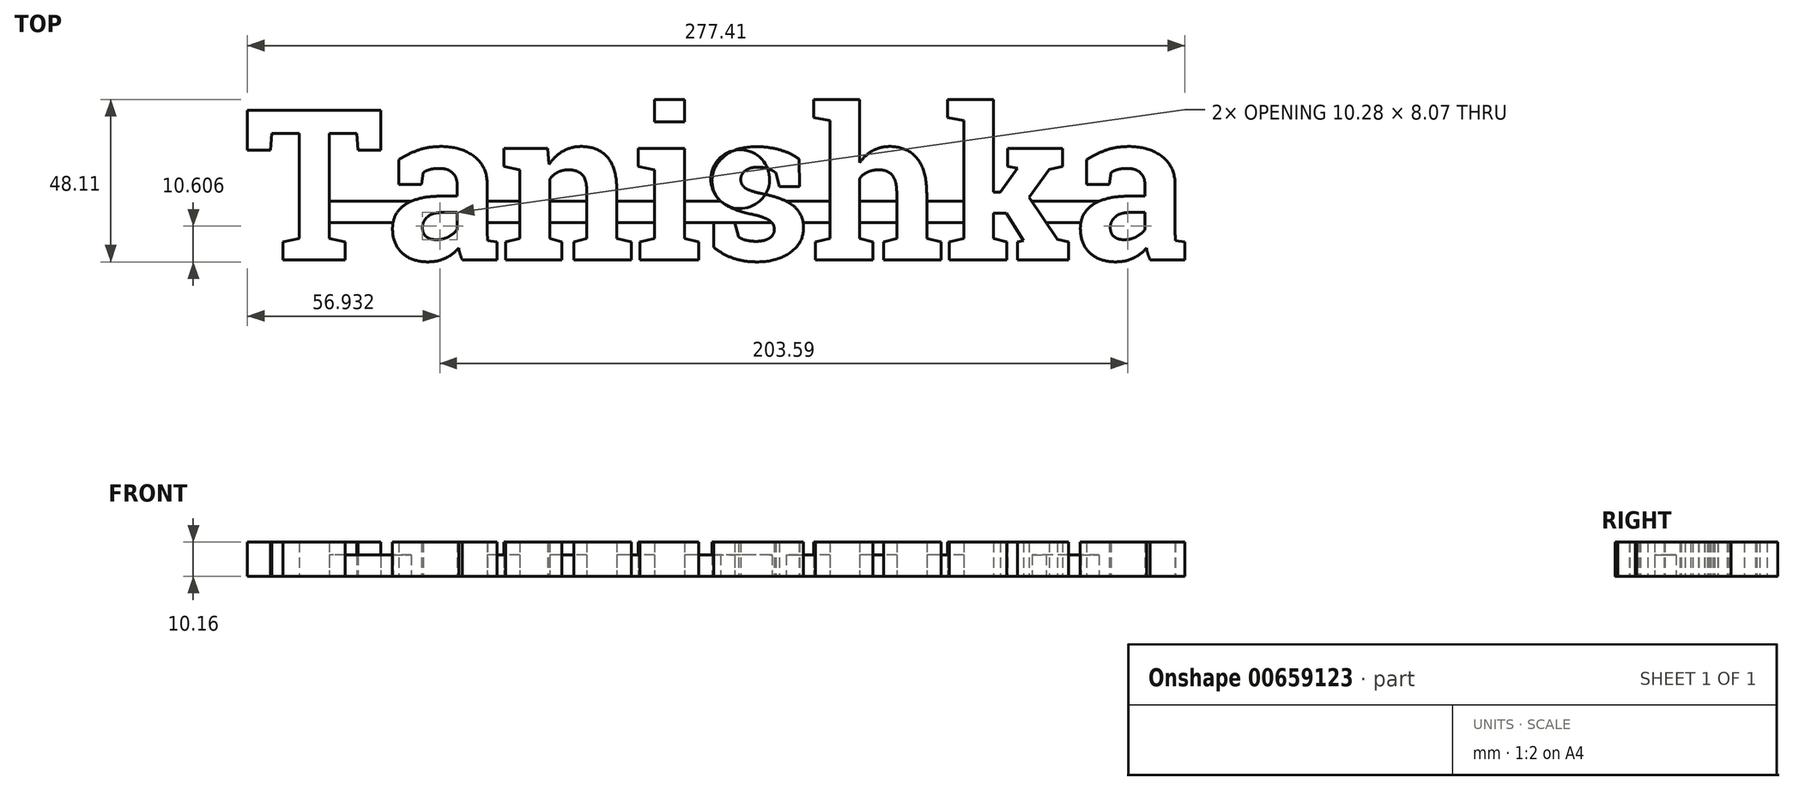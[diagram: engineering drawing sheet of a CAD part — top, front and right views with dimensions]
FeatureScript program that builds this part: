
annotation { "Feature Type Name" : "Feature", "Feature Type Description" : "" }
export const myFeature = defineFeature(function(context is Context, id is Id, definition is map)
    precondition{}
    {
        {
            var Q0;
            Q0=qCreatedBy(makeId("Top.planeOp"),FACE);
            var sketch = newSketch(context, id + "F0", { "sketchPlane" : qUnion([Q0])});
            skText(sketch, "E0", { "text": "Tanishka", "fontName": "RobotoSlab-Bold.ttf"});
            skLineSegment(sketch, "E1.bottom", {"start": v(206.32, -10.13) * mm, "end": v(-38.92, -10.13) * mm});
            skLineSegment(sketch, "E1.top", {"start": v(206.32, -3.78) * mm, "end": v(-38.92, -3.78) * mm});
            skLineSegment(sketch, "E1.left", {"start": v(206.32, -10.13) * mm, "end": v(206.32, -3.78) * mm});
            skLineSegment(sketch, "E1.right", {"start": v(-38.92, -10.13) * mm, "end": v(-38.92, -3.78) * mm});
            skPoint(sketch, "E1.middle", {"position": v(83.7, -6.96) * mm});
            skLineSegment(sketch, "E2.bottom", {"start": v(72.26, 26.44) * mm, "end": v(67.18, 26.44) * mm});
            skLineSegment(sketch, "E2.top", {"start": v(72.26, 10.06) * mm, "end": v(67.18, 10.06) * mm});
            skLineSegment(sketch, "E2.left", {"start": v(72.26, 26.44) * mm, "end": v(72.26, 10.06) * mm});
            skLineSegment(sketch, "E2.right", {"start": v(67.18, 26.44) * mm, "end": v(67.18, 10.06) * mm});
            const initialGuessF0  = {"E0": [-0.05753, -0.0211, 1, 0, 0.04487]};
            skSetInitialGuess(sketch, initialGuessF0);
            skSolve(sketch);
        }
        {
            var Q0;
            {var subQ0=sQuery(id+"F0.wireOp",EDGE,"E0.sketch_text.stroke-88");Q0=makeQuery(id+"F0.imprint","IMPRINT",FACE,{"disambiguationData":[TD([[makeQuery(id+"F0.imprint","IMPRINT",EDGE,{"derivedFrom":subQ0}),-1.0]])]});}
            var Q1;
            {var subQ0=sQuery(id+"F0.wireOp",EDGE,"E2.left");var subQ1=sQuery(id+"F0.wireOp",EDGE,"E0.sketch_text.stroke-87");var subQ2=makeQuery(id+"F0.imprint","INTERSECT",VERTEX,{"derivedFrom":[subQ1,subQ0]});Q1=makeQuery(id+"F0.imprint","IMPRINT",FACE,{"disambiguationData":[TD([[makeQuery(id+"F0.imprint","IMPRINT",EDGE,{"disambiguationData":[TD([[subQ2,-1.0]])],"derivedFrom":subQ1}),-1.0]])]});}
            var Q2;
            {var subQ0=sQuery(id+"F0.wireOp",EDGE,"E0.sketch_text.stroke-90");Q2=makeQuery(id+"F0.imprint","IMPRINT",FACE,{"disambiguationData":[TD([[makeQuery(id+"F0.imprint","IMPRINT",EDGE,{"derivedFrom":subQ0}),-1.0]])]});}
            var Q3;
            {var subQ5=sQuery(id+"F0.wireOp",EDGE,"E0.sketch_text.stroke-79");Q3=makeQuery(id+"F0.imprint","IMPRINT",FACE,{"disambiguationData":[TD([[makeQuery(id+"F0.imprint","IMPRINT",EDGE,{"derivedFrom":subQ5}),-1.0]])]});}
            var Q4;
            Q4=makeQuery(id+"F0.imprint","IMPRINT",FACE,{"disambiguationData":[TD([[makeQuery(id+"F0.imprint","IMPRINT",EDGE,{"derivedFrom":sQuery(id+"F0.wireOp",EDGE,"E0.sketch_text.stroke-0")}),-1.0]])]});
            var Q5;
            {var subQ5=sQuery(id+"F0.wireOp",EDGE,"E1.right");Q5=makeQuery(id+"F0.imprint","IMPRINT",FACE,{"disambiguationData":[TD([[makeQuery(id+"F0.imprint","IMPRINT",EDGE,{"derivedFrom":subQ5}),-1.0]])]});}
            var Q6;
            Q6=makeQuery(id+"F0.imprint","IMPRINT",FACE,{"disambiguationData":[TD([[makeQuery(id+"F0.imprint","IMPRINT",EDGE,{"derivedFrom":sQuery(id+"F0.wireOp",EDGE,"E0.sketch_text.stroke-16")}),-1.0]])]});
            var Q7;
            {var subQ0=sQuery(id+"F0.wireOp",EDGE,"E0.sketch_text.stroke-46");Q7=makeQuery(id+"F0.imprint","IMPRINT",FACE,{"disambiguationData":[TD([[makeQuery(id+"F0.imprint","IMPRINT",EDGE,{"derivedFrom":subQ0}),-1.0]])]});}
            var Q8;
            {var subQ0=sQuery(id+"F0.wireOp",EDGE,"E0.sketch_text.stroke-24");Q8=makeQuery(id+"F0.imprint","IMPRINT",FACE,{"disambiguationData":[TD([[makeQuery(id+"F0.imprint","IMPRINT",EDGE,{"derivedFrom":subQ0}),-1.0]])]});}
            var Q9;
            {var subQ10=sQuery(id+"F0.wireOp",EDGE,"E0.sketch_text.stroke-53");Q9=makeQuery(id+"F0.imprint","IMPRINT",FACE,{"disambiguationData":[TD([[makeQuery(id+"F0.imprint","IMPRINT",EDGE,{"derivedFrom":subQ10}),-1.0]])]});}
            var Q10;
            {var subQ5=sQuery(id+"F0.wireOp",EDGE,"E0.sketch_text.stroke-51");Q10=makeQuery(id+"F0.imprint","IMPRINT",FACE,{"disambiguationData":[TD([[makeQuery(id+"F0.imprint","IMPRINT",EDGE,{"derivedFrom":subQ5}),-1.0]])]});}
            var Q11;
            {var subQ0=sQuery(id+"F0.wireOp",EDGE,"E1.bottom");var subQ1=sQuery(id+"F0.wireOp",EDGE,"E0.sketch_text.stroke-52");var subQ2=makeQuery(id+"F0.imprint","INTERSECT",VERTEX,{"derivedFrom":[subQ1,subQ0]});Q11=makeQuery(id+"F0.imprint","IMPRINT",FACE,{"disambiguationData":[TD([[makeQuery(id+"F0.imprint","IMPRINT",EDGE,{"disambiguationData":[TD([[subQ2,-1.0]])],"derivedFrom":subQ1}),-1.0]])]});}
            var Q12;
            {var subQ0=sQuery(id+"F0.wireOp",EDGE,"E1.top");var subQ1=sQuery(id+"F0.wireOp",EDGE,"E0.sketch_text.stroke-61");var subQ2=makeQuery(id+"F0.imprint","INTERSECT",VERTEX,{"derivedFrom":[subQ1,subQ0]});Q12=makeQuery(id+"F0.imprint","IMPRINT",FACE,{"disambiguationData":[TD([[makeQuery(id+"F0.imprint","IMPRINT",EDGE,{"disambiguationData":[TD([[subQ2,-1.0]])],"derivedFrom":subQ1}),-1.0]])]});}
            var Q13;
            {var subQ0=sQuery(id+"F0.wireOp",EDGE,"E0.sketch_text.stroke-62");Q13=makeQuery(id+"F0.imprint","IMPRINT",FACE,{"disambiguationData":[TD([[makeQuery(id+"F0.imprint","IMPRINT",EDGE,{"derivedFrom":subQ0}),-1.0]])]});}
            var Q14;
            {var subQ0=sQuery(id+"F0.wireOp",EDGE,"E1.bottom");var subQ1=sQuery(id+"F0.wireOp",EDGE,"E0.sketch_text.stroke-78");var subQ2=makeQuery(id+"F0.imprint","INTERSECT",VERTEX,{"derivedFrom":[subQ1,subQ0]});Q14=makeQuery(id+"F0.imprint","IMPRINT",FACE,{"disambiguationData":[TD([[makeQuery(id+"F0.imprint","IMPRINT",EDGE,{"disambiguationData":[TD([[subQ2,-1.0]])],"derivedFrom":subQ1}),-1.0]])]});}
            var Q15;
            {var subQ2=sQuery(id+"F0.wireOp",EDGE,"E0.sketch_text.stroke-77");Q15=makeQuery(id+"F0.imprint","IMPRINT",FACE,{"disambiguationData":[TD([[makeQuery(id+"F0.imprint","IMPRINT",EDGE,{"derivedFrom":subQ2}),-1.0]])]});}
            var Q16;
            {var subQ5=sQuery(id+"F0.wireOp",EDGE,"E2.top");Q16=makeQuery(id+"F0.imprint","IMPRINT",FACE,{"disambiguationData":[TD([[makeQuery(id+"F0.imprint","IMPRINT",EDGE,{"derivedFrom":subQ5}),-1.0]])]});}
            var Q17;
            Q17=makeQuery(id+"F0.imprint","IMPRINT",FACE,{"disambiguationData":[TD([[makeQuery(id+"F0.imprint","IMPRINT",EDGE,{"derivedFrom":sQuery(id+"F0.wireOp",EDGE,"E0.sketch_text.stroke-91")}),-1.0]])]});
            var Q18;
            {var subQ11=sQuery(id+"F0.wireOp",EDGE,"E0.sketch_text.stroke-101");Q18=makeQuery(id+"F0.imprint","IMPRINT",FACE,{"disambiguationData":[TD([[makeQuery(id+"F0.imprint","IMPRINT",EDGE,{"derivedFrom":subQ11}),-1.0]])]});}
            var Q19;
            {var subQ0=sQuery(id+"F0.wireOp",EDGE,"E0.sketch_text.stroke-113");Q19=makeQuery(id+"F0.imprint","IMPRINT",FACE,{"disambiguationData":[TD([[makeQuery(id+"F0.imprint","IMPRINT",EDGE,{"derivedFrom":subQ0}),-1.0]])]});}
            var Q20;
            {var subQ4=sQuery(id+"F0.wireOp",EDGE,"E0.sketch_text.stroke-123");Q20=makeQuery(id+"F0.imprint","IMPRINT",FACE,{"disambiguationData":[TD([[makeQuery(id+"F0.imprint","IMPRINT",EDGE,{"derivedFrom":subQ4}),-1.0]])]});}
            var Q21;
            {var subQ0=sQuery(id+"F0.wireOp",EDGE,"E1.bottom");var subQ1=sQuery(id+"F0.wireOp",EDGE,"E0.sketch_text.stroke-122");var subQ2=makeQuery(id+"F0.imprint","INTERSECT",VERTEX,{"derivedFrom":[subQ1,subQ0]});Q21=makeQuery(id+"F0.imprint","IMPRINT",FACE,{"disambiguationData":[TD([[makeQuery(id+"F0.imprint","IMPRINT",EDGE,{"disambiguationData":[TD([[subQ2,-1.0]])],"derivedFrom":subQ1}),-1.0]])]});}
            var Q22;
            {var subQ5=sQuery(id+"F0.wireOp",EDGE,"E0.sketch_text.stroke-121");Q22=makeQuery(id+"F0.imprint","IMPRINT",FACE,{"disambiguationData":[TD([[makeQuery(id+"F0.imprint","IMPRINT",EDGE,{"derivedFrom":subQ5}),-1.0]])]});}
            var Q23;
            {var subQ0=sQuery(id+"F0.wireOp",EDGE,"E0.sketch_text.stroke-132");Q23=makeQuery(id+"F0.imprint","IMPRINT",FACE,{"disambiguationData":[TD([[makeQuery(id+"F0.imprint","IMPRINT",EDGE,{"derivedFrom":subQ0}),-1.0]])]});}
            var Q24;
            {var subQ0=sQuery(id+"F0.wireOp",EDGE,"E1.top");var subQ1=sQuery(id+"F0.wireOp",EDGE,"E0.sketch_text.stroke-131");var subQ2=makeQuery(id+"F0.imprint","INTERSECT",VERTEX,{"derivedFrom":[subQ1,subQ0]});Q24=makeQuery(id+"F0.imprint","IMPRINT",FACE,{"disambiguationData":[TD([[makeQuery(id+"F0.imprint","IMPRINT",EDGE,{"disambiguationData":[TD([[subQ2,-1.0]])],"derivedFrom":subQ1}),-1.0]])]});}
            var Q25;
            Q25=makeQuery(id+"F0.imprint","IMPRINT",FACE,{"disambiguationData":[TD([[makeQuery(id+"F0.imprint","IMPRINT",EDGE,{"derivedFrom":sQuery(id+"F0.wireOp",EDGE,"E0.sketch_text.stroke-147")}),-1.0]])]});
            var Q26;
            {var subQ0=sQuery(id+"F0.wireOp",EDGE,"E0.sketch_text.stroke-165");Q26=makeQuery(id+"F0.imprint","IMPRINT",FACE,{"disambiguationData":[TD([[makeQuery(id+"F0.imprint","IMPRINT",EDGE,{"derivedFrom":subQ0}),-1.0]])]});}
            var Q27;
            {var subQ0=sQuery(id+"F0.wireOp",EDGE,"E0.sketch_text.stroke-167");Q27=makeQuery(id+"F0.imprint","IMPRINT",FACE,{"disambiguationData":[TD([[makeQuery(id+"F0.imprint","IMPRINT",EDGE,{"derivedFrom":subQ0}),-1.0]])]});}
            var Q28;
            {var subQ0=sQuery(id+"F0.wireOp",EDGE,"E0.sketch_text.stroke-159");Q28=makeQuery(id+"F0.imprint","IMPRINT",FACE,{"disambiguationData":[TD([[makeQuery(id+"F0.imprint","IMPRINT",EDGE,{"derivedFrom":subQ0}),-1.0]])]});}
            var Q29;
            Q29=makeQuery(id+"F0.imprint","IMPRINT",FACE,{"disambiguationData":[TD([[makeQuery(id+"F0.imprint","IMPRINT",EDGE,{"derivedFrom":sQuery(id+"F0.wireOp",EDGE,"E0.sketch_text.stroke-174")}),-1.0]])]});
            var Q30;
            {var subQ0=sQuery(id+"F0.wireOp",EDGE,"E0.sketch_text.stroke-205");Q30=makeQuery(id+"F0.imprint","IMPRINT",FACE,{"disambiguationData":[TD([[makeQuery(id+"F0.imprint","IMPRINT",EDGE,{"derivedFrom":subQ0}),-1.0]])]});}
            extrude(context, id + "F1", {"entities" : qUnion([Q0, Q1, Q2, Q3, Q4, Q5, Q6, Q7, Q8, Q9, Q10, Q11, Q12, Q13, Q14, Q15, Q16, Q17, Q18, Q19, Q20, Q21, Q22, Q23, Q24, Q25, Q26, Q27, Q28, Q29, Q30]), "depth" : 10.16 * mm, "offsetDistance" : 25.4 * mm});
        }
        {
            var Q0;
            {var subQ1=sQuery(id+"F0.wireOp",EDGE,"E0.sketch_text.stroke-4");var subQ7=sQuery(id+"F0.wireOp",EDGE,"E1.top");var subQ9=makeQuery(id+"F0.imprint","INTERSECT",VERTEX,{"derivedFrom":[subQ1,subQ7]});Q0=makeQuery(id+"F0.imprint","IMPRINT",FACE,{"disambiguationData":[TD([[makeQuery(id+"F0.imprint","IMPRINT",EDGE,{"disambiguationData":[TD([[subQ9,-1.0]])],"derivedFrom":subQ1}),1.0]])]});}
            var Q1;
            {var subQ0=sQuery(id+"F0.wireOp",EDGE,"E1.top");var subQ1=sQuery(id+"F0.wireOp",EDGE,"E0.sketch_text.stroke-37");var subQ2=makeQuery(id+"F0.imprint","INTERSECT",VERTEX,{"derivedFrom":[subQ1,subQ0]});Q1=makeQuery(id+"F0.imprint","IMPRINT",FACE,{"disambiguationData":[TD([[makeQuery(id+"F0.imprint","IMPRINT",EDGE,{"disambiguationData":[TD([[subQ2,-1.0]])],"derivedFrom":subQ1}),1.0]])]});}
            var Q2;
            {var subQ0=sQuery(id+"F0.wireOp",EDGE,"E1.bottom");var subQ1=sQuery(id+"F0.wireOp",EDGE,"E0.sketch_text.stroke-67");var subQ2=makeQuery(id+"F0.imprint","INTERSECT",VERTEX,{"derivedFrom":[subQ1,subQ0]});Q2=makeQuery(id+"F0.imprint","IMPRINT",FACE,{"disambiguationData":[TD([[makeQuery(id+"F0.imprint","IMPRINT",EDGE,{"disambiguationData":[TD([[subQ2,-1.0]])],"derivedFrom":subQ1}),1.0]])]});}
            var Q3;
            {var subQ0=sQuery(id+"F0.wireOp",EDGE,"E1.top");var subQ1=sQuery(id+"F0.wireOp",EDGE,"E0.sketch_text.stroke-61");var subQ2=makeQuery(id+"F0.imprint","INTERSECT",VERTEX,{"derivedFrom":[subQ1,subQ0]});Q3=makeQuery(id+"F0.imprint","IMPRINT",FACE,{"disambiguationData":[TD([[makeQuery(id+"F0.imprint","IMPRINT",EDGE,{"disambiguationData":[TD([[subQ2,-1.0]])],"derivedFrom":subQ1}),1.0]])]});}
            var Q4;
            {var subQ5=sQuery(id+"F0.wireOp",EDGE,"E0.sketch_text.stroke-106");Q4=makeQuery(id+"F0.imprint","IMPRINT",FACE,{"disambiguationData":[TD([[makeQuery(id+"F0.imprint","IMPRINT",EDGE,{"derivedFrom":subQ5}),1.0]])]});}
            var Q5;
            {var subQ1=sQuery(id+"F0.wireOp",EDGE,"E0.sketch_text.stroke-100");var subQ5=sQuery(id+"F0.wireOp",EDGE,"E0.sketch_text.stroke-99");var subQ6=makeQuery(id+"F0.imprint","INTERSECT",VERTEX,{"derivedFrom":[subQ5,subQ1]});Q5=makeQuery(id+"F0.imprint","IMPRINT",FACE,{"disambiguationData":[TD([[makeQuery(id+"F0.imprint","IMPRINT",EDGE,{"disambiguationData":[TD([[subQ6,1.0]])],"derivedFrom":subQ5}),1.0]])]});}
            var Q6;
            {var subQ0=sQuery(id+"F0.wireOp",EDGE,"E1.bottom");var subQ1=sQuery(id+"F0.wireOp",EDGE,"E0.sketch_text.stroke-137");var subQ2=makeQuery(id+"F0.imprint","INTERSECT",VERTEX,{"derivedFrom":[subQ1,subQ0]});Q6=makeQuery(id+"F0.imprint","IMPRINT",FACE,{"disambiguationData":[TD([[makeQuery(id+"F0.imprint","IMPRINT",EDGE,{"disambiguationData":[TD([[subQ2,-1.0]])],"derivedFrom":subQ1}),1.0]])]});}
            var Q7;
            {var subQ0=sQuery(id+"F0.wireOp",EDGE,"E1.top");var subQ1=sQuery(id+"F0.wireOp",EDGE,"E0.sketch_text.stroke-131");var subQ2=makeQuery(id+"F0.imprint","INTERSECT",VERTEX,{"derivedFrom":[subQ1,subQ0]});Q7=makeQuery(id+"F0.imprint","IMPRINT",FACE,{"disambiguationData":[TD([[makeQuery(id+"F0.imprint","IMPRINT",EDGE,{"disambiguationData":[TD([[subQ2,-1.0]])],"derivedFrom":subQ1}),1.0]])]});}
            var Q8;
            {var subQ1=sQuery(id+"F0.wireOp",EDGE,"E0.sketch_text.stroke-158");var subQ7=sQuery(id+"F0.wireOp",EDGE,"E1.top");var subQ9=makeQuery(id+"F0.imprint","INTERSECT",VERTEX,{"derivedFrom":[subQ1,subQ7]});Q8=makeQuery(id+"F0.imprint","IMPRINT",FACE,{"disambiguationData":[TD([[makeQuery(id+"F0.imprint","IMPRINT",EDGE,{"disambiguationData":[TD([[subQ9,-1.0]])],"derivedFrom":subQ1}),1.0]])]});}
            extrude(context, id + "F2", {"entities" : qUnion([Q0, Q1, Q2, Q3, Q4, Q5, Q6, Q7, Q8]), "depth" : 6.35 * mm, "offsetDistance" : 25.4 * mm});
        }
    });
